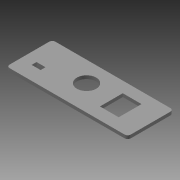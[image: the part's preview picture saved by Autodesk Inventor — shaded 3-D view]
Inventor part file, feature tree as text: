
AUTODESK INVENTOR PART (.ipt)
format: ipt  version: 2016 (Build 200138000, 138)  size: 130,560 bytes
history: native  units: mm
features: extrude x3, sketch x3, fillet x1
ambient origin geometry x8: Origin, YZ Plane, XZ Plane, XY Plane, X Axis, Y Axis, Z Axis, Center Point
bodies: Solid1 (feature_tree)
feature tree (7):
  extrude  "Extrusion1"  Depth=22.5mm
  fillet  "Fillet1"  Radius=1.6mm
  extrude  "Extrusion2"  Depth=1.5mm
  extrude  "Extrusion4"  Depth=10.0mm
  sketch  "Sketch1"  dims[d0=59.5mm d1=22.5mm d2=1.6mm d3=0.0mm]
  sketch  "Sketch2"  dims[d4=1.5mm d5=9.5mm]
  sketch  "Sketch4"  dims[d6=10.0mm d7=0.0mm d15=12.51mm d16=26.801mm d17=6.01mm d18=1.401mm d19=4.4mm d20=2.4mm d21=6.35mm d22=2.0mm d23=6.01mm d24=1.401mm d25=9.2mm d26=11.2mm d28=43.18mm d29=0.1mm d30=10.0mm d31=0.0mm]
